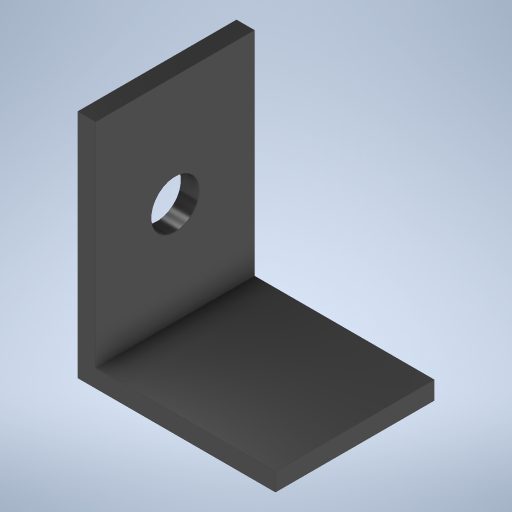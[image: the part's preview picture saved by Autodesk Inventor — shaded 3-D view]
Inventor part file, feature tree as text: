
AUTODESK INVENTOR PART (.ipt)
format: ipt  version: 2023 (Build 270158000, 158)  size: 234,496 bytes
history: native  units: mm
features: sketch x3, extrude x2, hole x1
ambient origin geometry x8: Origin, YZ Plane, XZ Plane, XY Plane, X Axis, Y Axis, Z Axis, Center Point
bodies: Volumenkörper1 (feature_tree)
feature tree (6):
  extrude  "Extrusion1"  Depth=26.5mm
  extrude  "Extrusion2"  Depth=35.5mm
  hole  "Bohrung1"  [1 undecoded]
  sketch  "Skizze1"  dims[d0=38.5mm d1=26.5mm]
  sketch  "Skizze2"  dims[d2=33.0mm d3=0.0mm d4=35.5mm]
  sketch  "Skizze3"  dims[d5=0.0mm d6=0.0mm d7=8.0mm d8=6.0mm d9=4.0mm d10=2.0mm d11=90.0deg d12=8.0mm d13=20.594885mm d14=0.0mm d15=17.0mm]
note: 1 required parameter value undecoded (feature->parameter linkage not recoverable at this tier; creation-order binding heuristic only, values carry confidence <= 0.55)
